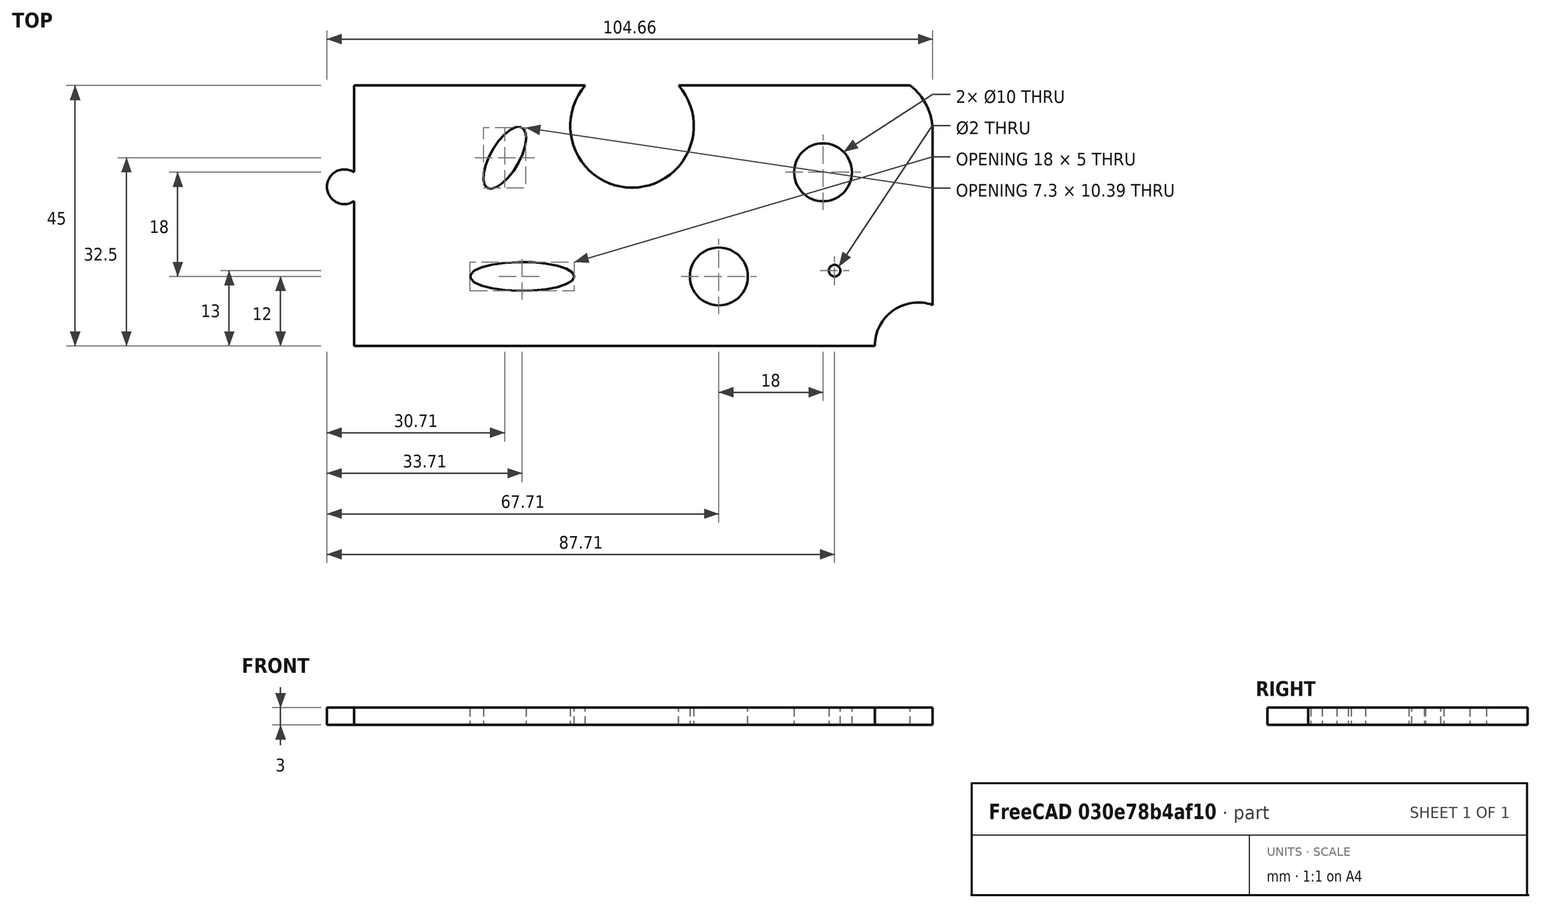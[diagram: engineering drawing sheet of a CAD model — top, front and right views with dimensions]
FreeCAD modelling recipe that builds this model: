
FCSTD DOCUMENT  (FreeCAD 0.19R16203 (Git))
Label: Drilling_0
License: CreativeCommons Attribution
LicenseURL: http://creativecommons.org/licenses/by/4.0/
objects: Sketcher::SketchObject×1, PartDesign::Pad×1, PartDesign::Body×1
note: 4 computed .brp shape members not serialized (recipe doc carries the construction recipe); baked Part::Feature solids carry a one-line shape summary decoded from their .brp

FEATURE [Sketcher::SketchObject] Sketch
  MapMode = 5
  Support = -> [XY_Plane]
  sketch-geometry (23):
    g0: LineSegment StartX=-48.0468 StartY=-20 StartZ=0 EndX=41.9532 EndY=-20 EndZ=0
    g1: ArcOfCircle CenterX=49.4532 CenterY=-20 CenterZ=0 NormalX=0 NormalY=0 NormalZ=1 AngleXU=0 Radius=7.5 StartAngle=1.23096 EndAngle=3.14159
    g2: LineSegment StartX=51.9532 StartY=-12.9289 StartZ=0 EndX=51.9532 EndY=17.0711 EndZ=0
    g3: ArcOfCircle CenterX=41.9532 CenterY=17.0711 CenterZ=0 NormalX=0 NormalY=0 NormalZ=1 AngleXU=0 Radius=10 StartAngle=1e-16 EndAngle=0.915542
    g4: LineSegment StartX=48.0468 StartY=25 StartZ=0 EndX=8.0468 EndY=25 EndZ=0
    g5: ArcOfCircle CenterX=0 CenterY=18 CenterZ=0 NormalX=0 NormalY=0 NormalZ=1 AngleXU=0 Radius=10.6654 StartAngle=2.42565 EndAngle=6.99913
    g6: LineSegment StartX=-8.0468 StartY=25 StartZ=0 EndX=-48.0468 EndY=25 EndZ=0
    g7: LineSegment StartX=-48.0468 StartY=25 StartZ=0 EndX=-48.0468 EndY=10 EndZ=0
    g8: ArcOfCircle CenterX=-49.7051 CenterY=7.5 CenterZ=0 NormalX=0 NormalY=0 NormalZ=1 AngleXU=0 Radius=3 StartAngle=0.985111 EndAngle=5.29807
    g9: LineSegment StartX=-48.0468 StartY=5 StartZ=0 EndX=-48.0468 EndY=-20 EndZ=0
    g10: Circle CenterX=33 CenterY=10 CenterZ=0 NormalX=0 NormalY=0 NormalZ=1 AngleXU=0 Radius=5
    g11: Circle CenterX=35 CenterY=-7 CenterZ=0 NormalX=0 NormalY=0 NormalZ=1 AngleXU=0 Radius=1
    g12: Ellipse CenterX=-19 CenterY=-8 CenterZ=0 NormalX=0 NormalY=0 NormalZ=1 MajorRadius=9 MinorRadius=2.5 AngleXU=0
    g13: LineSegment [constr] StartX=-10 StartY=-8 StartZ=0 EndX=-28 EndY=-8 EndZ=0
    g14: LineSegment [constr] StartX=-19 StartY=-5.5 StartZ=0 EndX=-19 EndY=-10.5 EndZ=0
    g15: GeomPoint X=-10.3542 Y=-8 Z=0
    g16: GeomPoint X=-27.6458 Y=-8 Z=0
    g17: Ellipse CenterX=-22 CenterY=12.5 CenterZ=0 NormalX=0 NormalY=0 NormalZ=1 MajorRadius=6 MinorRadius=2.5 AngleXU=-2.0944
    g18: LineSegment [constr] StartX=-25 StartY=7.30385 StartZ=0 EndX=-19 EndY=17.6962 EndZ=0
    g19: LineSegment [constr] StartX=-19.8349 StartY=11.25 StartZ=0 EndX=-24.1651 EndY=13.75 EndZ=0
    g20: GeomPoint X=-24.7272 Y=7.77639 Z=0
    g21: GeomPoint X=-19.2728 Y=17.2236 Z=0
    g22: Circle CenterX=15 CenterY=-8 CenterZ=0 NormalX=0 NormalY=0 NormalZ=1 AngleXU=0 Radius=5
  constraints (53):
    c: Horizontal(g0)
    c: Perpendicular(g0,g1) = 4.71239
    c: Coincident(g1,g2)
    c: Vertical(g2)
    c: Tangent(g2,g3) = -1.5708
    c: Coincident(g3,g4)
    c: Horizontal(g4)
    c: Coincident(g5,g6)
    c: Horizontal(g6)
    c: Coincident(g6,g7)
    c: Vertical(g7)
    c: Coincident(g8,g9)
    c: Coincident(g9,g0)
    c: Vertical(g9)
    c: PointOnObject(g7,g9)
    c: Coincident(g7,g8)
    c: Coincident(g4,g5)
    c: PointOnObject(g5,g4)
    c: InternalAlignment(g13-g16 -> g12) x4
    c: InternalAlignment(g18-g21 -> g17) x4
    c: Diameter(g10) = 10
    c: Diameter(g11) = 2
    c: Distance(g14) = 5
    c: Distance(g13) = 18
    c: Horizontal(g13)
    c: Distance(g18) = 12
    c: Distance(g19) = 5
    c: Radius(g1) = 7.5
    c: Radius(g3) = 10
    c: Radius(g8) = 3
    c: DistanceY(g7,g7) = 15
    c: DistanceY(g9,g9) = 25
    c: DistanceY(g0,g6) = 45
    c: DistanceX(g0,g1) = 100
    c: DistanceX(g0,g0) = 90
    c: DistanceY(g2,g2) = 30
    c: Equal(g6,g4)
    c: DistanceX(g6,g6) = 40
    c: DistanceY(g5,g4) = 7
    c: DistanceX(g17) = -22
    c: DistanceY(g17) = 12.5
    c: DistanceX(g12) = -19
    c: DistanceY(g12) = -8
    c: DistanceX(g10) = 33
    c: DistanceY(g10) = 10
    c: DistanceX(g11) = 35
    c: DistanceY(g11) = -7
    c: DistanceX(g5) = 0
    c: DistanceY(g5) = 18
    c: Angle(g18) = 1.0472
    c: Equal(g22,g10)
    c: DistanceX(g22) = 15
    c: DistanceY(g22) = -8
FEATURE [PartDesign::Pad] Pad
  Length = 3
  Length2 = 100
  Profile = -> Sketch
  Type = 0
FEATURE [PartDesign::Body] Body  label="Drilling_0"
  Group = -> [Sketch,Pad]
  Origin = -> Origin
  Tip = -> Pad
